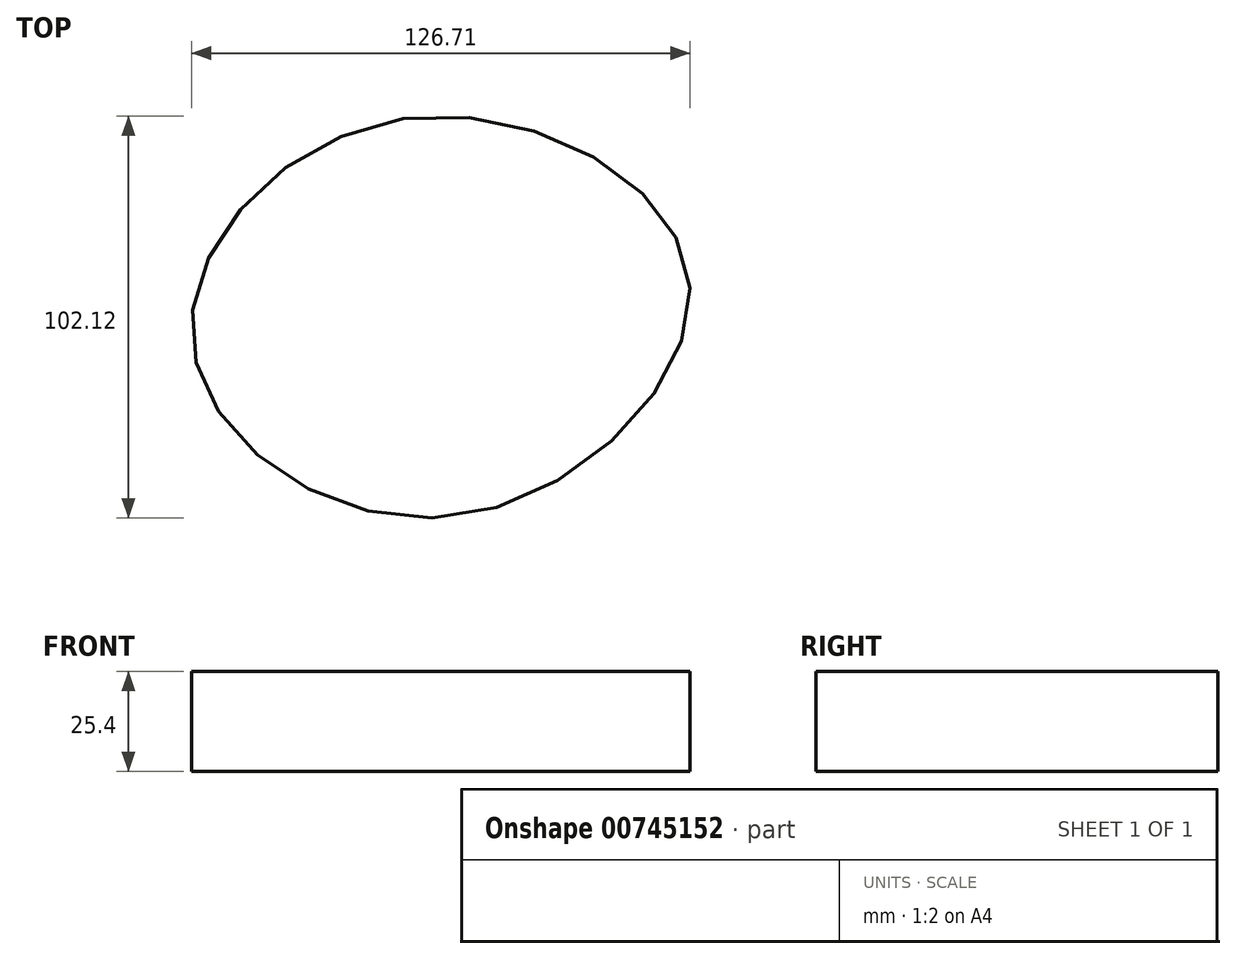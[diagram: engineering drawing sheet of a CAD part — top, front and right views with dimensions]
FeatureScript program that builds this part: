
annotation { "Feature Type Name" : "Feature", "Feature Type Description" : "" }
export const myFeature = defineFeature(function(context is Context, id is Id, definition is map)
    precondition{}
    {
        {
            var Q0;
            Q0=qCreatedBy(makeId("Top.planeOp"),FACE);
            var sketch = newSketch(context, id + "F0", { "sketchPlane" : qUnion([Q0])});
            skFitSpline(sketch, "E0", {"points": [v(53.57, 40.4) * mm, v(126.22, 0) * mm, v(65.84, -60.67) * mm, v(0, -16.7) * mm, v(53.57, 40.4) * mm]});
            skSolve(sketch);
        }
        {
            var Q0;
            Q0 = qSketchRegion(id + "F0", true);
            extrude(context, id + "F1", {"entities" : qUnion([Q0]), "depth" : 25.4 * mm, "offsetDistance" : 25.4 * mm});
        }
    });
